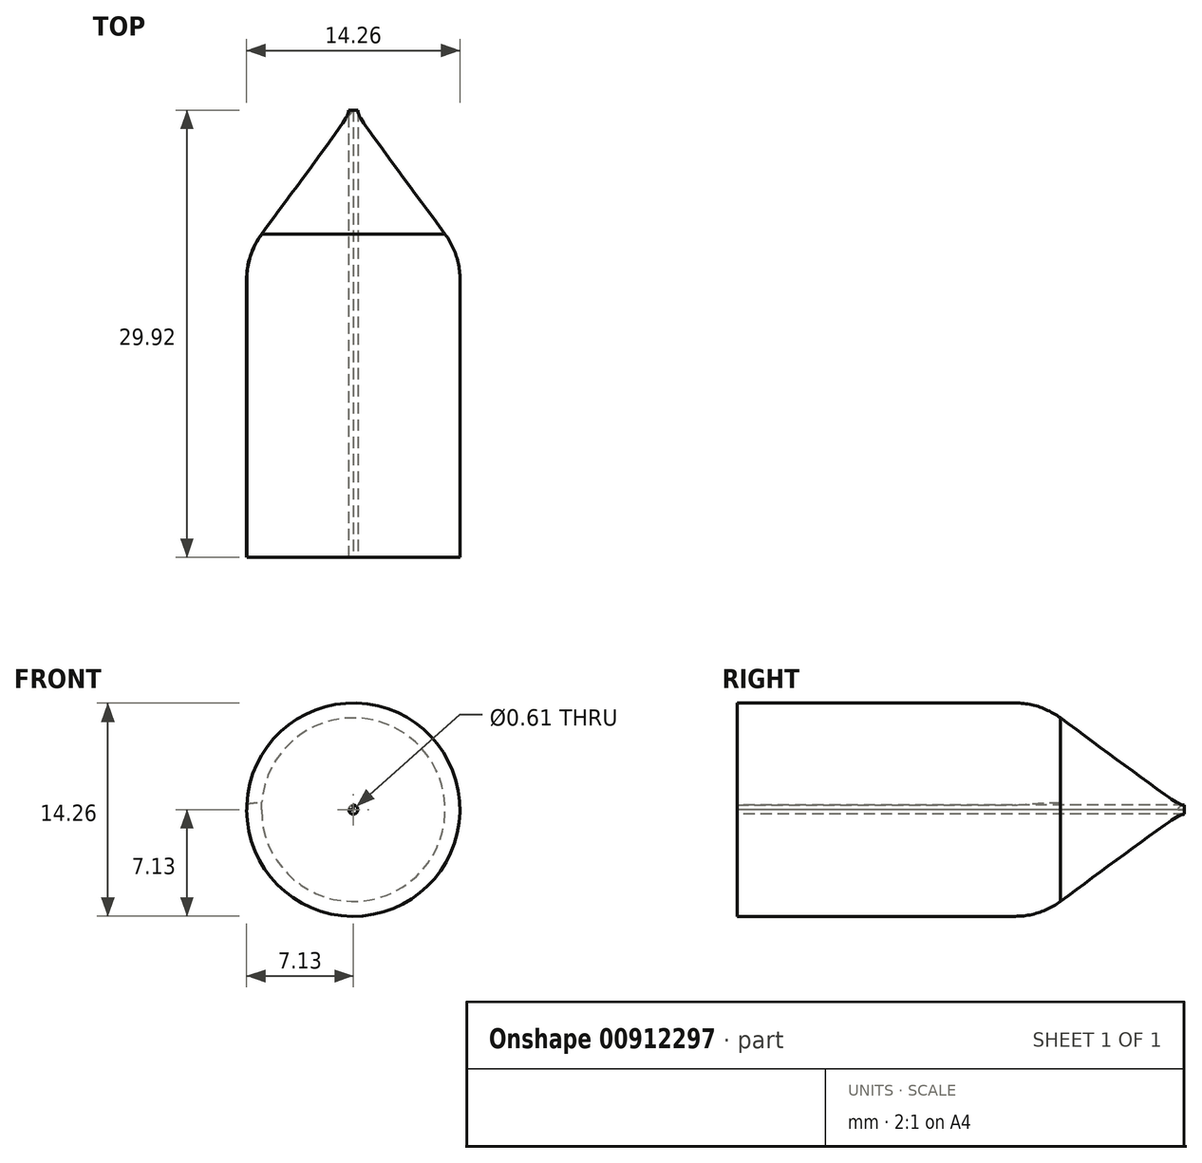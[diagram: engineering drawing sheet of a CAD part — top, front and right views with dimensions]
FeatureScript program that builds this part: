
annotation { "Feature Type Name" : "Feature", "Feature Type Description" : "" }
export const myFeature = defineFeature(function(context is Context, id is Id, definition is map)
    precondition{}
    {
        {
            var Q0;
            Q0=qCreatedBy(makeId("Top.planeOp"),FACE);
            var sketch = newSketch(context, id + "F0", { "sketchPlane" : qUnion([Q0])});
            skLineSegment(sketch, "E0", {"start": v(-7.13, -10.04) * mm, "end": v(-7.13, 10.24) * mm});
            skLineSegment(sketch, "E1", {"start": v(-7.13, 10.24) * mm, "end": v(0, 19.88) * mm});
            skLineSegment(sketch, "E2", {"start": v(-7.13, -10.04) * mm, "end": v(0, -10.04) * mm});
            skLineSegment(sketch, "E3", {"start": v(0, 19.88) * mm, "end": v(0, -10.04) * mm});
            skSolve(sketch);
        }
        {
            var Q0;
            Q0=qCreatedBy(makeId("Right.planeOp"),FACE);
            var sketch = newSketch(context, id + "F1", { "sketchPlane" : qUnion([Q0])});
            skLineSegment(sketch, "E4", {"start": v(-10.34, 0) * mm, "end": v(19.58, 0) * mm});
            skSolve(sketch);
        }
        {
            var Q0;
            Q0=makeQuery(id+"F0.imprint","IMPRINT",FACE,{"disambiguationData":[TD([[makeQuery(id+"F0.imprint","IMPRINT",EDGE,{"derivedFrom":sQuery(id+"F0.wireOp",EDGE,"E0")}),-1.0]])]});
            extrude(context, id + "F2", {"entities" : qUnion([Q0]), "depth" : 0.3 * mm, "offsetDistance" : 25.4 * mm});
        }
        {
            var Q0;
            Q0=makeQuery(id+"F2.opExtrude","CAP_FACE",FACE,{"disambiguationData":[OSD([sQuery(id+"F0.wireOp",EDGE,"E0"),sQuery(id+"F0.wireOp",EDGE,"E1"),sQuery(id+"F0.wireOp",EDGE,"E2"),sQuery(id+"F0.wireOp",EDGE,"E3")])],"isStart":false});
            var Q1;
            Q1=sQuery(id+"F1.wireOp",EDGE,"E4");
            revolve(context, id + "F3", {"operationType" : NewBodyOperationType.ADD, "surfaceOperationType" : NewSurfaceOperationType.NEW, "entities" : qUnion([Q0]), "axis" : qUnion([Q1]), "revolveType" : RevolveType.FULL});
        }
        {
            var Q0;
            Q0=makeQuery(id+"F3.boolean.opBoolean","SPLIT",EDGE,{"derivedFrom":makeQuery(id+"F3.opRevolve","SWEPT_EDGE",EDGE,{"disambiguationData":[OSD([sQuery(id+"F0.wireOp",EDGE,"E0"),sQuery(id+"F0.wireOp",EDGE,"E1")])]})});
            fillet(context, id + "F4", {"entities" : qUnion([Q0]), "radius" : 5.08 * mm, "tangentPropagation" : true, "allowEdgeOverflow" : false});
        }
    });
